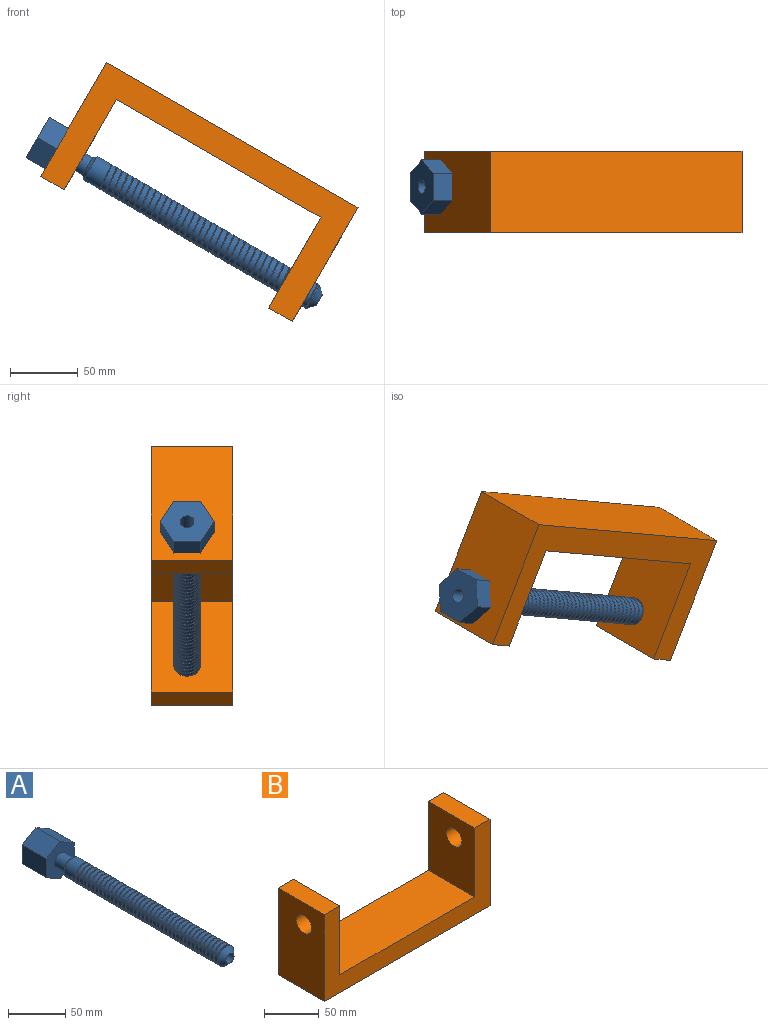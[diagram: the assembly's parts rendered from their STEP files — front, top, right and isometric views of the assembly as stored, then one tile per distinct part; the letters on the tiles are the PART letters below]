
ASSEMBLY  parts=2 mates=1
PART A: 53 faces, bbox 34.6x240x40 mm
  f0: plane 30x20mm, normal (1,0,0), area 600mm2, adj f1,f5,f6,f7
  f1: plane 30x17.32mm, normal (0.5,0,0.87), area 600mm2, adj f0,f2,f6,f7
  f2: plane 30x17.32mm, normal (-0.5,0,0.87), area 600mm2, adj f1,f3,f6,f7
  f3: plane 30x20mm, normal (-1,0,0), area 600mm2, adj f2,f4,f6,f7
  f4: plane 30x17.32mm, normal (-0.5,0,-0.87), area 600mm2, adj f3,f5,f6,f7
  f5: plane 30x17.32mm, normal (0.5,0,-0.87), area 600mm2, adj f0,f4,f6,f7
  f6: plane 40x34.64mm, normal (0,-1,0), area 862.5mm2, adj f0,f1,f2,f3,f4,f5,f8
  f7: plane 40x34.64mm, normal (0,1,0), area 960.7mm2, adj f0,f1,f2,f3,f4,f5,f52
  f8: cylinder r=7.5mm len=15mm, axis (0,1,0), area 589mm2, adj f6,f47
  f9: cylinder r=10mm len=20mm, axis (0,1,0), area 937.1mm2, adj f46,f47,f49,f50,f51
  f10: cylinder r=10mm len=20mm, axis (0,1,0), area 144mm2, adj f11,f48,f50,f51
  f11: cylinder r=10mm len=20mm, axis (0,1,0), area 242.2mm2, adj f10,f12,f50,f51
  f12: cylinder r=10mm len=20mm, axis (0,1,0), area 242.2mm2, adj f11,f13,f50,f51
  f13: cylinder r=10mm len=20mm, axis (0,1,0), area 242.3mm2, adj f12,f14,f50,f51
  f14: cylinder r=10mm len=20mm, axis (0,1,0), area 242.2mm2, adj f13,f15,f50,f51
  f15: cylinder r=10mm len=20mm, axis (0,1,0), area 242.3mm2, adj f14,f16,f50,f51
  f16: cylinder r=10mm len=20mm, axis (0,1,0), area 242.2mm2, adj f15,f17,f50,f51
  f17: cylinder r=10mm len=20mm, axis (0,1,0), area 242.2mm2, adj f16,f18,f50,f51
  f18: cylinder r=10mm len=20mm, axis (0,1,0), area 242.2mm2, adj f17,f19,f50,f51
  f19: cylinder r=10mm len=20mm, axis (0,1,0), area 242.2mm2, adj f18,f20,f50,f51
  f20: cylinder r=10mm len=20mm, axis (0,1,0), area 242.2mm2, adj f19,f21,f50,f51
  f21: cylinder r=10mm len=20mm, axis (0,1,0), area 242.2mm2, adj f20,f22,f50,f51
  f22: cylinder r=10mm len=20mm, axis (0,1,0), area 242.2mm2, adj f21,f23,f50,f51
  f23: cylinder r=10mm len=20mm, axis (0,1,0), area 242.2mm2, adj f22,f24,f50,f51
  f24: cylinder r=10mm len=20mm, axis (0,1,0), area 242.2mm2, adj f23,f25,f50,f51
  f25: cylinder r=10mm len=20mm, axis (0,1,0), area 242.2mm2, adj f24,f26,f50,f51
  f26: cylinder r=10mm len=20mm, axis (0,1,0), area 242.2mm2, adj f25,f27,f50,f51
  f27: cylinder r=10mm len=20mm, axis (0,1,0), area 242.2mm2, adj f26,f28,f50,f51
  f28: cylinder r=10mm len=20mm, axis (0,1,0), area 242.2mm2, adj f27,f29,f50,f51
  f29: cylinder r=10mm len=20mm, axis (0,1,0), area 242.2mm2, adj f28,f30,f50,f51
  f30: cylinder r=10mm len=20mm, axis (0,1,0), area 242.2mm2, adj f29,f31,f50,f51
  f31: cylinder r=10mm len=20mm, axis (0,1,0), area 242.2mm2, adj f30,f32,f50,f51
  f32: cylinder r=10mm len=20mm, axis (0,1,0), area 242.2mm2, adj f31,f33,f50,f51
  f33: cylinder r=10mm len=20mm, axis (0,1,0), area 242.2mm2, adj f32,f34,f50,f51
  f34: cylinder r=10mm len=20mm, axis (0,1,0), area 242.2mm2, adj f33,f35,f50,f51
  f35: cylinder r=10mm len=20mm, axis (0,1,0), area 242.2mm2, adj f34,f36,f50,f51
  f36: cylinder r=10mm len=20mm, axis (0,1,0), area 242.3mm2, adj f35,f37,f50,f51
  f37: cylinder r=10mm len=20mm, axis (0,1,0), area 242.2mm2, adj f36,f38,f50,f51
  f38: cylinder r=10mm len=20mm, axis (0,1,0), area 242.3mm2, adj f37,f39,f50,f51
  f39: cylinder r=10mm len=20mm, axis (0,1,0), area 242.2mm2, adj f38,f40,f50,f51
  f40: cylinder r=10mm len=20mm, axis (0,1,0), area 242.2mm2, adj f39,f41,f50,f51
  f41: cylinder r=10mm len=20mm, axis (0,1,0), area 242.2mm2, adj f40,f42,f50,f51
  f42: cylinder r=10mm len=20mm, axis (0,1,0), area 242.2mm2, adj f41,f43,f50,f51
  f43: cylinder r=10mm len=20mm, axis (0,1,0), area 242.2mm2, adj f42,f44,f50,f51
  f44: cylinder r=10mm len=20mm, axis (0,1,0), area 242.2mm2, adj f43,f45,f50,f51
  f45: cylinder r=10mm len=20mm, axis (0,1,0), area 242.2mm2, adj f44,f46,f50,f51
  f46: cylinder r=10mm len=20mm, axis (0,1,0), area 242.2mm2, adj f9,f45,f50,f51
  f47: cone r=10mm half-angle=45deg, axis (0,-1,0), area 194.4mm2, adj f8,f9
  f48: cone r=5mm half-angle=45deg, axis (0,1,0), area 326mm2, adj f10,f50,f51,f52
  f49: plane 0.9x0.9mm, normal (0,0,-1), area 0.4mm2, adj f9,f50,f51
  f50: bspline ~184.31x31.33mm, area 2294.1mm2, adj f9,f10,f11,f12,f13,f14,f15,f16
  f51: bspline ~184.31x31.33mm, area 2290.3mm2, adj f9,f10,f11,f12,f13,f14,f15,f16
  f52: cylinder r=5mm len=240mm, axis (0,1,0), area 7539.8mm2, adj f7,f48
PART B: 12 faces, bbox 214.5x60x97.2 mm
  f0: plane 97.17x60mm, normal (-1,0,0), area 5516mm2, adj f1,f7,f8,f9,f10
  f1: plane 214.49x60mm, normal (0,0,-1), area 12869.6mm2, adj f0,f2,f8,f9
  f2: plane 97.17x60mm, normal (1,0,0), area 5516mm2, adj f1,f3,f8,f9,f11
  f3: plane 60x20mm, normal (0,0,1), area 1200mm2, adj f2,f4,f8,f9
  f4: plane 77.17x60mm, normal (-1,0,0), area 4316mm2, adj f3,f5,f8,f9,f11
  f5: plane 174.49x60mm, normal (0,0,1), area 10469.6mm2, adj f4,f6,f8,f9
  f6: plane 77.17x60mm, normal (1,0,0), area 4316mm2, adj f5,f7,f8,f9,f10
  f7: plane 60x20mm, normal (0,0,1), area 1200mm2, adj f0,f6,f8,f9
  f8: plane 214.49x97.17mm, normal (0,-1,0), area 7376.7mm2, adj f0,f1,f2,f3,f4,f5,f6,f7
  f9: plane 214.49x97.17mm, normal (0,1,0), area 7376.7mm2, adj f0,f1,f2,f3,f4,f5,f6,f7
  f10: cylinder r=10mm len=20mm, axis (1,0,0), area 1256.6mm2, adj f0,f6
  f11: cylinder r=10mm len=20mm, axis (1,0,0), area 1256.6mm2, adj f2,f4
PLACE A rot(axis=(0.77,-0.45,0.45),104.5deg) t=(-88.87,89.38,150.15)mm
PLACE B rot(axis=(0.97,0,-0.26),180deg) t=(44.86,55.75,134.77)mm fixed
MATE slider A.f8 <-> B.f10  axis (-0.87,0,0.5) through (-57.47,89.38,132.02)mm
